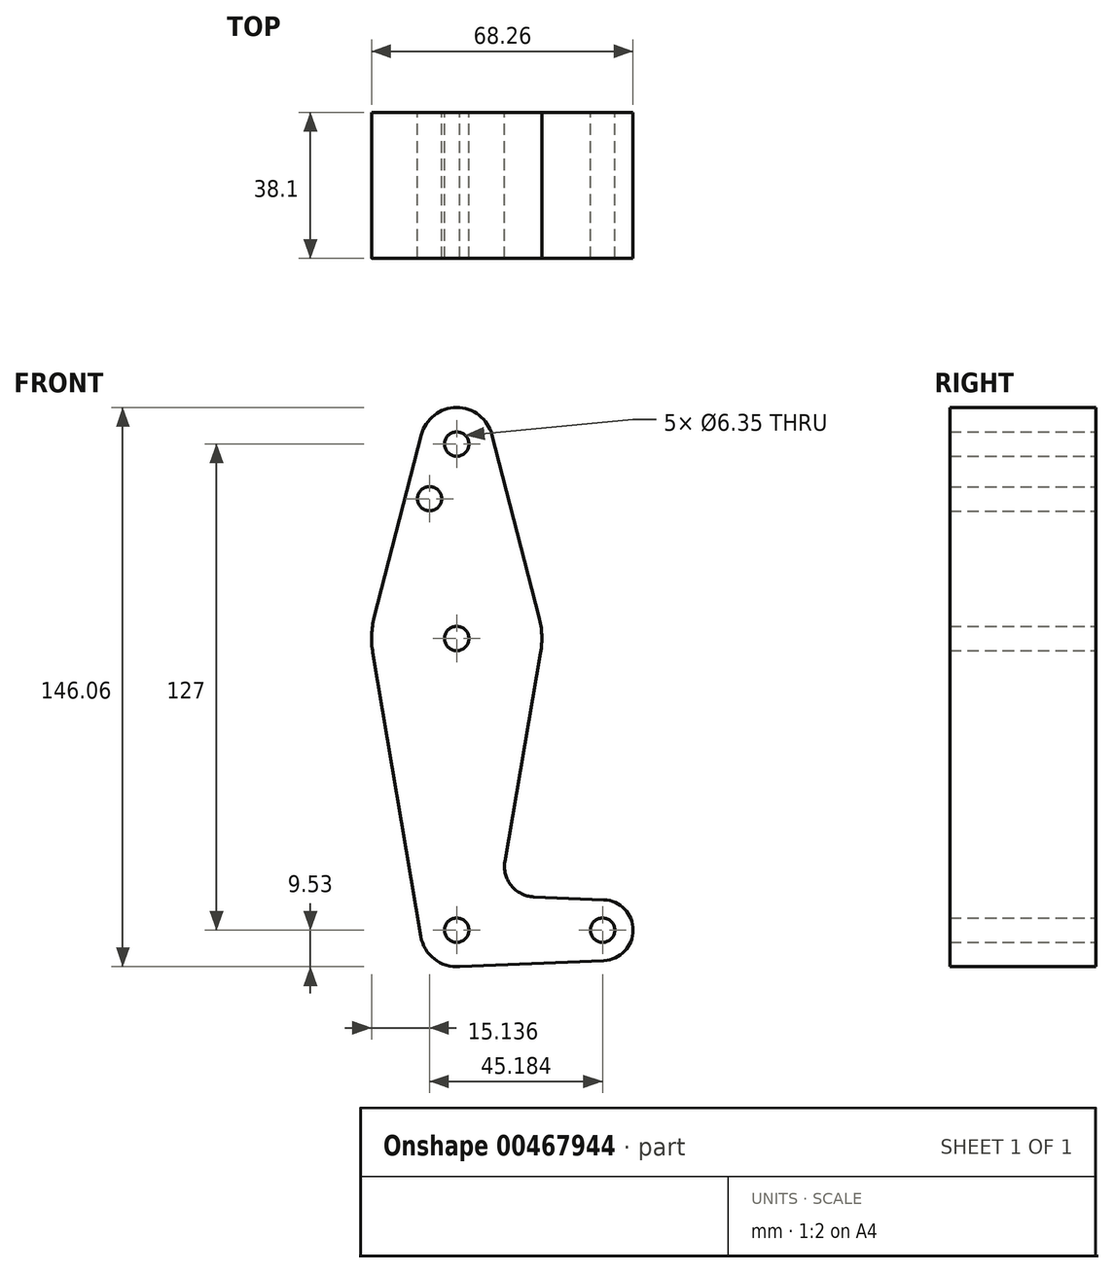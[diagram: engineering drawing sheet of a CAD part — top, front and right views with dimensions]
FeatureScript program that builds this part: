
annotation { "Feature Type Name" : "Feature", "Feature Type Description" : "" }
export const myFeature = defineFeature(function(context is Context, id is Id, definition is map)
    precondition{}
    {
        {
            var Q0;
            Q0=qCreatedBy(makeId("Front.planeOp"),FACE);
            var sketch = newSketch(context, id + "F0", { "sketchPlane" : qUnion([Q0])});
            skCircle(sketch, "E0", {"center": v(0, 76.2) * mm, "radius": 9.52 * mm});
            skCircle(sketch, "E1", {"center": v(0, -50.8) * mm, "radius": 9.53 * mm});
            skCircle(sketch, "E2", {"center": v(0, 25.4) * mm, "radius": 22.23 * mm});
            skCircle(sketch, "E3", {"center": v(38.1, -50.8) * mm, "radius": 7.94 * mm});
            skLineSegment(sketch, "E4", {"start": v(0, -50.8) * mm, "end": v(38.1, -50.8) * mm, "construction": true});
            skLineSegment(sketch, "E5", {"start": v(0, 76.2) * mm, "end": v(0, -50.8) * mm, "construction": true});
            skCircle(sketch, "E6", {"center": v(0, 25.4) * mm, "radius": 3.18 * mm});
            skCircle(sketch, "E7", {"center": v(0, 76.2) * mm, "radius": 3.18 * mm});
            skCircle(sketch, "E8", {"center": v(0, -50.8) * mm, "radius": 3.18 * mm});
            skCircle(sketch, "E9", {"center": v(38.1, -50.8) * mm, "radius": 3.18 * mm});
            skLineSegment(sketch, "E10", {"start": v(-9.22, 78.58) * mm, "end": v(-21.52, 30.96) * mm});
            skLineSegment(sketch, "E11", {"start": v(-21.91, 21.7) * mm, "end": v(-9.4, -52.39) * mm});
            skLineSegment(sketch, "E12", {"start": v(9.22, 78.58) * mm, "end": v(21.52, 30.96) * mm});
            skLineSegment(sketch, "E13", {"start": v(21.9, 21.66) * mm, "end": v(12.6, -32.83) * mm});
            skLineSegment(sketch, "E14", {"start": v(20.1, -42.1) * mm, "end": v(38.43, -42.87) * mm});
            skLineSegment(sketch, "E15", {"start": v(0, -60.33) * mm, "end": v(38.43, -58.73) * mm});
            skPoint(sketch, "E16.newPointB", {"position": v(0, -41.28) * mm});
            skArc(sketch, "E16.filletArc", {"start": v(12.6, -32.83) * mm, "mid": v(14.25, -39.16) * mm, "end": v(20.1, -42.1) * mm});
            skCircle(sketch, "E17", {"center": v(-7.08, 61.93) * mm, "radius": 3.18 * mm});
            skCircle(sketch, "E18", {"center": v(-7.08, 61.93) * mm, "radius": 1.59 * mm});
            skSolve(sketch);
        }
        {
            var Q0;
            Q0 = qSketchRegion(id + "F0", true);
            extrude(context, id + "F1", {"entities" : qUnion([Q0]), "endBound" : BoundingType.SYMMETRIC, "depth" : 25.4 * mm});
        }
        {
            var Q0;
            Q0 = qSketchRegion(id + "F0", true);
            extrude(context, id + "F2", {"entities" : qUnion([Q0]), "operationType" : NewBodyOperationType.ADD, "depth" : 25.4 * mm, "offsetDistance" : 25.4 * mm});
        }
    });
